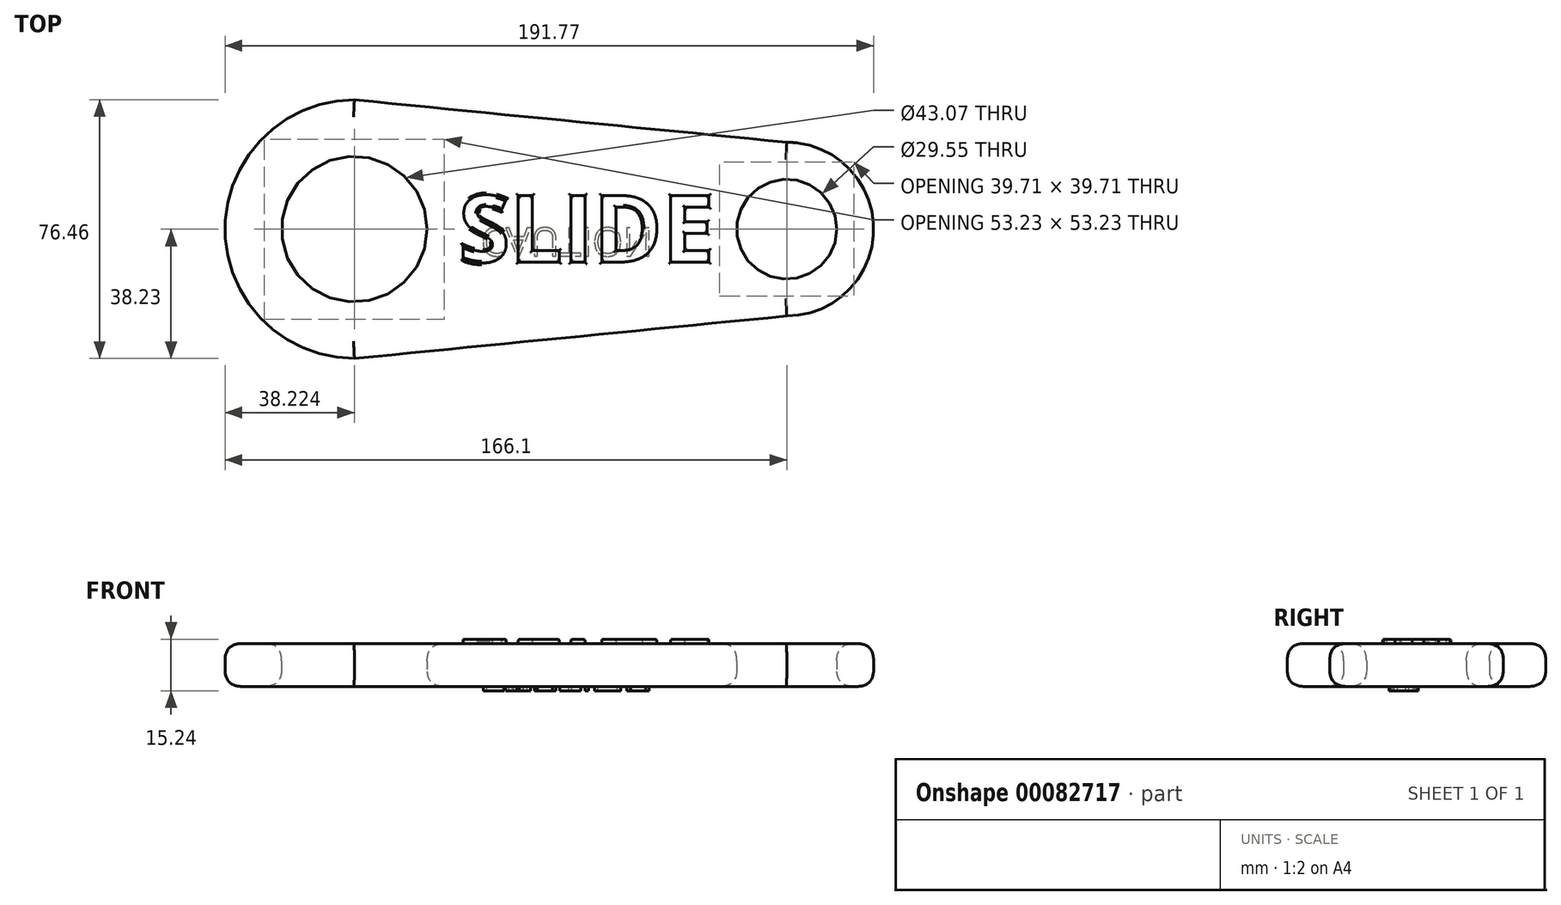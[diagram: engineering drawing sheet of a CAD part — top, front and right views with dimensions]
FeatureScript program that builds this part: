
annotation { "Feature Type Name" : "Feature", "Feature Type Description" : "" }
export const myFeature = defineFeature(function(context is Context, id is Id, definition is map)
    precondition{}
    {
        {
            var Q0;
            Q0=qCreatedBy(makeId("Top.planeOp"),FACE);
            var sketch = newSketch(context, id + "F0", { "sketchPlane" : qUnion([Q0])});
            skLineSegment(sketch, "E0", {"start": v(0, 0) * mm, "end": v(-127.88, 0) * mm, "construction": true});
            skArc(sketch, "E1", {"start": v(-127.88, 38.23) * mm, "mid": v(-166.1, 0) * mm, "end": v(-127.88, -38.23) * mm});
            skArc(sketch, "E2", {"start": v(0, -25.67) * mm, "mid": v(25.67, 0) * mm, "end": v(0, 25.67) * mm});
            skLineSegment(sketch, "E3", {"start": v(-127.88, 43.96) * mm, "end": v(-127.88, -53.37) * mm, "construction": true});
            skLineSegment(sketch, "E4", {"start": v(0, 33.14) * mm, "end": v(0, -41.96) * mm, "construction": true});
            skLineSegment(sketch, "E5", {"start": v(-127.88, 38.23) * mm, "end": v(0, 25.67) * mm});
            skLineSegment(sketch, "E6.MirrorCS", {"start": v(-127.88, -38.23) * mm, "end": v(0, -25.67) * mm});
            skCircle(sketch, "E7", {"center": v(-127.88, 0) * mm, "radius": 21.53 * mm});
            skCircle(sketch, "E8", {"center": v(0, 0) * mm, "radius": 14.77 * mm});
            skSolve(sketch);
        }
        {
            var Q0;
            Q0 = qSketchRegion(id + "FuZnPTuPabT5Wvj_0", true);
            var Q1;
            Q1=makeQuery(id+"F0.imprint","IMPRINT",FACE,{"disambiguationData":[TD([[makeQuery(id+"F0.imprint","IMPRINT",EDGE,{"derivedFrom":sQuery(id+"F0.wireOp",EDGE,"E1")}),1.0]])]});
            extrude(context, id + "F1", {"entities" : qUnion([Q0, Q1]), "endBound" : BoundingType.SYMMETRIC, "depth" : 12.7 * mm});
        }
        {
            var Q0;
            Q0=makeQuery(id+"F1.opExtrude","CAP_EDGE",EDGE,{"disambiguationData":[OSD([sQuery(id+"F0.wireOp",EDGE,"E7")])],"isStart":false});
            var Q1;
            Q1=makeQuery(id+"F1.opExtrude","CAP_EDGE",EDGE,{"disambiguationData":[OSD([sQuery(id+"F0.wireOp",EDGE,"E8")])],"isStart":false});
            var Q2;
            Q2=makeQuery(id+"F1.opExtrude","CAP_EDGE",EDGE,{"disambiguationData":[OSD([sQuery(id+"F0.wireOp",EDGE,"E7")])],"isStart":true});
            var Q3;
            Q3=makeQuery(id+"F1.opExtrude","CAP_EDGE",EDGE,{"disambiguationData":[OSD([sQuery(id+"F0.wireOp",EDGE,"E8")])],"isStart":true});
            var Q4;
            Q4=makeQuery(id+"F1.opExtrude","CAP_EDGE",EDGE,{"disambiguationData":[OSD([sQuery(id+"F0.wireOp",EDGE,"E1")])],"isStart":false});
            var Q5;
            Q5=makeQuery(id+"F1.opExtrude","CAP_EDGE",EDGE,{"disambiguationData":[OSD([sQuery(id+"F0.wireOp",EDGE,"E5")])],"isStart":false});
            var Q6;
            Q6=makeQuery(id+"F1.opExtrude","CAP_EDGE",EDGE,{"disambiguationData":[OSD([sQuery(id+"F0.wireOp",EDGE,"E2")])],"isStart":false});
            var Q7;
            Q7=makeQuery(id+"F1.opExtrude","CAP_EDGE",EDGE,{"disambiguationData":[OSD([sQuery(id+"F0.wireOp",EDGE,"E6.MirrorCS")])],"isStart":false});
            var Q8;
            Q8=makeQuery(id+"F1.opExtrude","CAP_EDGE",EDGE,{"disambiguationData":[OSD([sQuery(id+"F0.wireOp",EDGE,"E1")])],"isStart":true});
            var Q9;
            Q9=makeQuery(id+"F1.opExtrude","CAP_EDGE",EDGE,{"disambiguationData":[OSD([sQuery(id+"F0.wireOp",EDGE,"E6.MirrorCS")])],"isStart":true});
            var Q10;
            Q10=makeQuery(id+"F1.opExtrude","CAP_EDGE",EDGE,{"disambiguationData":[OSD([sQuery(id+"F0.wireOp",EDGE,"E2")])],"isStart":true});
            var Q11;
            Q11=makeQuery(id+"F1.opExtrude","CAP_EDGE",EDGE,{"disambiguationData":[OSD([sQuery(id+"F0.wireOp",EDGE,"E5")])],"isStart":true});
            fillet(context, id + "F2", {"entities" : qUnion([Q0, Q1, Q2, Q3, Q4, Q5, Q6, Q7, Q8, Q9, Q10, Q11]), "radius" : 5.08 * mm, "tangentPropagation" : true, "rho" : 0.5, "crossSection" : FilletCrossSection.CONIC, "allowEdgeOverflow" : false});
        }
        {
            var Q0;
            Q0=makeQuery(id+"F1.opExtrude","CAP_FACE",FACE,{"disambiguationData":[OSD([sQuery(id+"F0.wireOp",EDGE,"E1"),sQuery(id+"F0.wireOp",EDGE,"E2"),sQuery(id+"F0.wireOp",EDGE,"E5"),sQuery(id+"F0.wireOp",EDGE,"E6.MirrorCS"),sQuery(id+"F0.wireOp",EDGE,"E7"),sQuery(id+"F0.wireOp",EDGE,"E8")])],"isStart":false});
            var sketch = newSketch(context, id + "F3", { "sketchPlane" : qUnion([Q0])});
            skText(sketch, "E9", { "text": "SLIDE", "fontName": "OpenSans-Bold.ttf"});
            const initialGuessF3  = {"E9": [-0.09703, -0.00975, 1, 0, 0.01982]};
            skSetInitialGuess(sketch, initialGuessF3);
            skSolve(sketch);
        }
        {
            var Q0;
            Q0 = qSketchRegion(id + "F3", true);
            extrude(context, id + "F4", {"entities" : qUnion([Q0]), "operationType" : NewBodyOperationType.ADD, "depth" : 1.27 * mm});
        }
        {
            var Q0;
            Q0=makeQuery(id+"F1.opExtrude","CAP_FACE",FACE,{"disambiguationData":[OSD([sQuery(id+"F0.wireOp",EDGE,"E1"),sQuery(id+"F0.wireOp",EDGE,"E2"),sQuery(id+"F0.wireOp",EDGE,"E5"),sQuery(id+"F0.wireOp",EDGE,"E6.MirrorCS"),sQuery(id+"F0.wireOp",EDGE,"E7"),sQuery(id+"F0.wireOp",EDGE,"E8")])],"isStart":true});
            var sketch = newSketch(context, id + "F5", { "sketchPlane" : qUnion([Q0])});
            skText(sketch, "E10", { "text": "CAUTION\n", "fontName": "OpenSans-Regular.ttf"});
            const initialGuessF5  = {"E10": [-0.09051, -0.0004, 1, 0, 0.00841]};
            skSetInitialGuess(sketch, initialGuessF5);
            skSolve(sketch);
        }
        {
            var Q0;
            Q0 = qSketchRegion(id + "F5", true);
            extrude(context, id + "F6", {"entities" : qUnion([Q0]), "operationType" : NewBodyOperationType.ADD, "depth" : 1.27 * mm});
        }
        {
            var Q0;
            {var subQ0=sQuery(id+"F0.wireOp",EDGE,"E2");var subQ1=sQuery(id+"F0.wireOp",EDGE,"E8");var subQ2=sQuery(id+"F0.wireOp",EDGE,"E7");var subQ3=sQuery(id+"F0.wireOp",EDGE,"E5");var subQ4=sQuery(id+"F0.wireOp",EDGE,"E6.MirrorCS");var subQ5=sQuery(id+"F0.wireOp",EDGE,"E1");Q0=makeQuery(id+"F4.boolean.opBoolean","SPLIT",FACE,{"disambiguationData":[TD([makeQuery(id+"F4.opExtrude","SWEPT_FACE",FACE,{"disambiguationData":[OSD([sQuery(id+"F3.wireOp",EDGE,"E9.sketch_text.stroke-0")])]})])],"derivedFrom":makeQuery(id+"F1.opExtrude","CAP_FACE",FACE,{"disambiguationData":[OSD([subQ5,subQ0,subQ3,subQ4,subQ2,subQ1])],"isStart":false})});}
            var Q1;
            Q1=makeQuery(id+"F4.opExtrude","CAP_FACE",FACE,{"disambiguationData":[OSD([sQuery(id+"F3.wireOp",EDGE,"E9.sketch_text.stroke-0"),sQuery(id+"F3.wireOp",EDGE,"E9.sketch_text.stroke-1"),sQuery(id+"F3.wireOp",EDGE,"E9.sketch_text.stroke-2"),sQuery(id+"F3.wireOp",EDGE,"E9.sketch_text.stroke-3"),sQuery(id+"F3.wireOp",EDGE,"E9.sketch_text.stroke-4"),sQuery(id+"F3.wireOp",EDGE,"E9.sketch_text.stroke-5"),sQuery(id+"F3.wireOp",EDGE,"E9.sketch_text.stroke-6"),sQuery(id+"F3.wireOp",EDGE,"E9.sketch_text.stroke-7"),sQuery(id+"F3.wireOp",EDGE,"E9.sketch_text.stroke-8"),sQuery(id+"F3.wireOp",EDGE,"E9.sketch_text.stroke-9"),sQuery(id+"F3.wireOp",EDGE,"E9.sketch_text.stroke-10"),sQuery(id+"F3.wireOp",EDGE,"E9.sketch_text.stroke-11"),sQuery(id+"F3.wireOp",EDGE,"E9.sketch_text.stroke-12"),sQuery(id+"F3.wireOp",EDGE,"E9.sketch_text.stroke-13"),sQuery(id+"F3.wireOp",EDGE,"E9.sketch_text.stroke-14"),sQuery(id+"F3.wireOp",EDGE,"E9.sketch_text.stroke-15"),sQuery(id+"F3.wireOp",EDGE,"E9.sketch_text.stroke-16"),sQuery(id+"F3.wireOp",EDGE,"E9.sketch_text.stroke-17"),sQuery(id+"F3.wireOp",EDGE,"E9.sketch_text.stroke-18"),sQuery(id+"F3.wireOp",EDGE,"E9.sketch_text.stroke-19"),sQuery(id+"F3.wireOp",EDGE,"E9.sketch_text.stroke-20"),sQuery(id+"F3.wireOp",EDGE,"E9.sketch_text.stroke-21"),sQuery(id+"F3.wireOp",EDGE,"E9.sketch_text.stroke-22"),sQuery(id+"F3.wireOp",EDGE,"E9.sketch_text.stroke-23"),sQuery(id+"F3.wireOp",EDGE,"E9.sketch_text.stroke-24"),sQuery(id+"F3.wireOp",EDGE,"E9.sketch_text.stroke-25"),sQuery(id+"F3.wireOp",EDGE,"E9.sketch_text.stroke-26"),sQuery(id+"F3.wireOp",EDGE,"E9.sketch_text.stroke-27")])],"isStart":false});
            var Q2;
            Q2=makeQuery(id+"F4.opExtrude","CAP_FACE",FACE,{"disambiguationData":[OSD([sQuery(id+"F3.wireOp",EDGE,"E9.sketch_text.stroke-28"),sQuery(id+"F3.wireOp",EDGE,"E9.sketch_text.stroke-29"),sQuery(id+"F3.wireOp",EDGE,"E9.sketch_text.stroke-30"),sQuery(id+"F3.wireOp",EDGE,"E9.sketch_text.stroke-31"),sQuery(id+"F3.wireOp",EDGE,"E9.sketch_text.stroke-32"),sQuery(id+"F3.wireOp",EDGE,"E9.sketch_text.stroke-33")])],"isStart":false});
            var Q3;
            Q3=makeQuery(id+"F4.opExtrude","CAP_FACE",FACE,{"disambiguationData":[OSD([sQuery(id+"F3.wireOp",EDGE,"E9.sketch_text.stroke-34"),sQuery(id+"F3.wireOp",EDGE,"E9.sketch_text.stroke-35"),sQuery(id+"F3.wireOp",EDGE,"E9.sketch_text.stroke-36"),sQuery(id+"F3.wireOp",EDGE,"E9.sketch_text.stroke-37")])],"isStart":false});
            var Q4;
            Q4=makeQuery(id+"F4.opExtrude","CAP_FACE",FACE,{"disambiguationData":[OSD([sQuery(id+"F3.wireOp",EDGE,"E9.sketch_text.stroke-50"),sQuery(id+"F3.wireOp",EDGE,"E9.sketch_text.stroke-51"),sQuery(id+"F3.wireOp",EDGE,"E9.sketch_text.stroke-52"),sQuery(id+"F3.wireOp",EDGE,"E9.sketch_text.stroke-53"),sQuery(id+"F3.wireOp",EDGE,"E9.sketch_text.stroke-54"),sQuery(id+"F3.wireOp",EDGE,"E9.sketch_text.stroke-55"),sQuery(id+"F3.wireOp",EDGE,"E9.sketch_text.stroke-56"),sQuery(id+"F3.wireOp",EDGE,"E9.sketch_text.stroke-57"),sQuery(id+"F3.wireOp",EDGE,"E9.sketch_text.stroke-58"),sQuery(id+"F3.wireOp",EDGE,"E9.sketch_text.stroke-59"),sQuery(id+"F3.wireOp",EDGE,"E9.sketch_text.stroke-60"),sQuery(id+"F3.wireOp",EDGE,"E9.sketch_text.stroke-61")])],"isStart":false});
            var Q5;
            Q5=makeQuery(id+"F4.opExtrude","CAP_FACE",FACE,{"disambiguationData":[OSD([sQuery(id+"F3.wireOp",EDGE,"E9.sketch_text.stroke-38"),sQuery(id+"F3.wireOp",EDGE,"E9.sketch_text.stroke-39"),sQuery(id+"F3.wireOp",EDGE,"E9.sketch_text.stroke-40"),sQuery(id+"F3.wireOp",EDGE,"E9.sketch_text.stroke-41"),sQuery(id+"F3.wireOp",EDGE,"E9.sketch_text.stroke-42"),sQuery(id+"F3.wireOp",EDGE,"E9.sketch_text.stroke-43"),sQuery(id+"F3.wireOp",EDGE,"E9.sketch_text.stroke-44"),sQuery(id+"F3.wireOp",EDGE,"E9.sketch_text.stroke-45"),sQuery(id+"F3.wireOp",EDGE,"E9.sketch_text.stroke-46"),sQuery(id+"F3.wireOp",EDGE,"E9.sketch_text.stroke-47"),sQuery(id+"F3.wireOp",EDGE,"E9.sketch_text.stroke-48"),sQuery(id+"F3.wireOp",EDGE,"E9.sketch_text.stroke-49")])],"isStart":false});
            fillet(context, id + "F7", {"entities" : qUnion([Q0, Q1, Q2, Q3, Q4, Q5]), "radius" : 0.5 * mm, "tangentPropagation" : true, "allowEdgeOverflow" : false});
        }
    });
